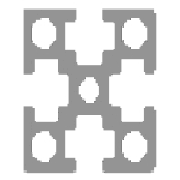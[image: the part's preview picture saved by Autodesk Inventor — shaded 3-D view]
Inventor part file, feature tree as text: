
AUTODESK INVENTOR PART (.ipt)
format: ipt  version: 2018.2 (Build 222227000, 227)  size: 262,656 bytes
history: native  units: mm
features: other x2, extrude x1
ambient origin geometry x8: Origin, YZ Plane, XZ Plane, XY Plane, X Axis, Y Axis, Z Axis, Center Point
bodies: Body1 (feature_tree)
feature tree (3):
  other  "開始平面"
  other  "終了平面"
  extrude  "ボディ"  Depth=4.0mm
